# Revit family: Faucet-Deck_Mount-Bath-KOHLER-Castia-K-T35911_1
name_source: partatom
category: Plumbing Fixtures
units: mm (PartAtom-declared; Revit-internal decimal feet)

## family parameters
Cut with Voids When Loaded = No
Host = Face
OmniClass Number = 23.31.11.00
OmniClass Title = Faucets
Part Type = Normal
Room Calculation Point = No
Round Connector Dimension = Use Diameter
Shared = No

## types (5) — shared parameters
ADA Compliant = No
Assembly Code = D2010
CW Connection = Yes
Cold Water Inlet = Cold Water Inlet
Date Modified = 04/18/2023
Default Elevation = 36"
Description = Two Hanldle Deck Mount Bath Filler Non Divert
Drain Included = No
Flow Rate = 0 GPM
HW Connection = Yes
Handle Clearance = 2 3/4"
Height = 7 5/16"
Hot Water Inlet = Hot Water Inlet
Length = 7 1/2"
Manufacturer = Kohler Co.
Master Format 2014 = 22 41 39
Master Format 2014 Name = Residential Faucets, Supplies, and Trim
Material = Premium Metal Construction
Pressure = 0.00 psi
Product Documentation Link = https://www.us.kohler.com
Product Name = Castia
Product Page URL = http://www.us.kohler.com
Spout Reach = 7 1/2"
URL = https://www.us.kohler.com
Vent Connection = No
Waste Connection = No
Waste Water Outlet = Waste Water Outlet
WaterSense Certified = No

## per-type parameters (varying)
| type | Finish | Model | Type |
| 2MB-Vibrant Brushed Moderne Brass | Kohler-Metal-2MB-Vibrant_Brushed_Moderne_Brass | K-T35911-4-2MB | 1 |
| BL-Matte Black | Kohler-Metal-BL-Matte_Black | K-T35911-4-BL | 2 |
| BN-Vibrant Brushed Nickel | Kohler-Metal-BN-Vibrant_Brushed_Nickel | K-T35911-4-BN | 3 |
| CP-Polished Chrome | Kohler-Metal-CP-Polished_Chrome | K-T35911-4-CP | 4 |
| SN-Vibrant Polished Nickel | Kohler-Metal-SN-Vibrant_Polished_Nickel | K-T35911-4-SN | 5 |

## geometry (parser evidence)
native form markers: Sweep x7
no freeform markers — native parametric forms only
